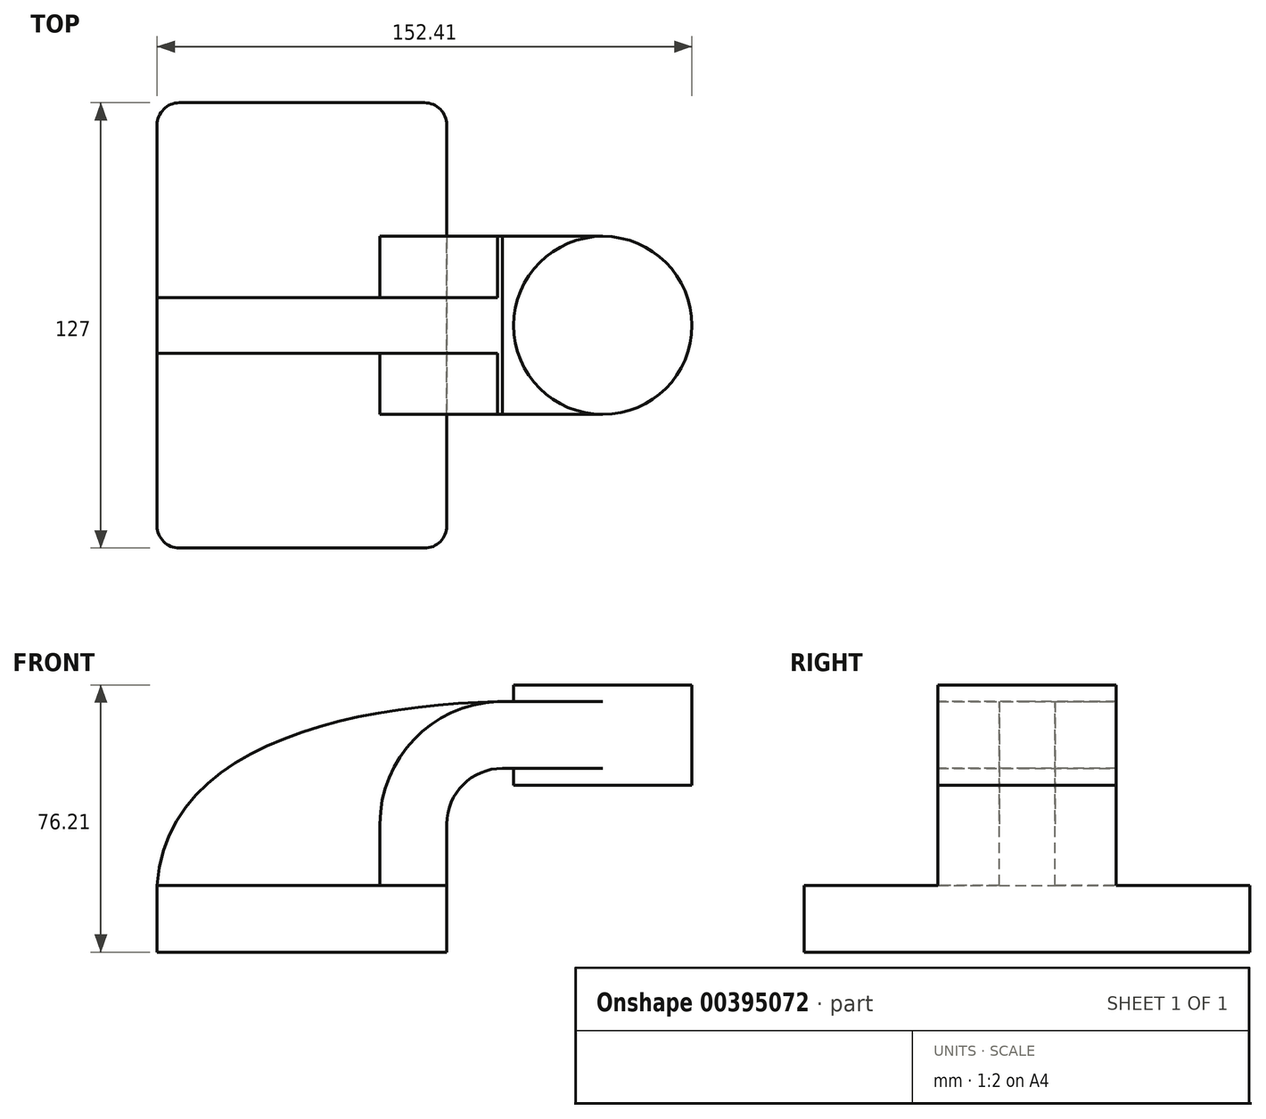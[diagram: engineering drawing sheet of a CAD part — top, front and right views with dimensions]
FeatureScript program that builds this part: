
annotation { "Feature Type Name" : "Feature", "Feature Type Description" : "" }
export const myFeature = defineFeature(function(context is Context, id is Id, definition is map)
    precondition{}
    {
        {
            var Q0;
            Q0=qCreatedBy(makeId("Front.planeOp"),FACE);
            var sketch = newSketch(context, id + "F0", { "sketchPlane" : qUnion([Q0])});
            skLineSegment(sketch, "E0.bottom", {"start": v(41.28, -9.52) * mm, "end": v(-41.27, -9.52) * mm});
            skLineSegment(sketch, "E0.top", {"start": v(41.27, 9.53) * mm, "end": v(-41.28, 9.53) * mm});
            skLineSegment(sketch, "E0.left", {"start": v(41.28, -9.52) * mm, "end": v(41.28, 9.53) * mm});
            skLineSegment(sketch, "E0.right", {"start": v(-41.27, -9.52) * mm, "end": v(-41.28, 9.52) * mm});
            skPoint(sketch, "E0.middle", {"position": v(0, 0) * mm});
            skLineSegment(sketch, "E1.bottom", {"start": v(111.12, 66.68) * mm, "end": v(60.32, 66.68) * mm});
            skLineSegment(sketch, "E1.top", {"start": v(111.12, 38.1) * mm, "end": v(60.33, 38.1) * mm});
            skLineSegment(sketch, "E1.left", {"start": v(111.12, 66.68) * mm, "end": v(111.12, 38.1) * mm});
            skLineSegment(sketch, "E1.right", {"start": v(60.32, 66.68) * mm, "end": v(60.33, 38.1) * mm});
            skPoint(sketch, "E1.middle", {"position": v(85.73, 52.39) * mm});
            skLineSegment(sketch, "E2", {"start": v(41.27, 9.53) * mm, "end": v(41.27, 27) * mm});
            skArc(sketch, "E3", {"start": v(41.27, 27) * mm, "mid": v(45.92, 38.23) * mm, "end": v(57.15, 42.88) * mm});
            skLineSegment(sketch, "E4", {"start": v(57.15, 42.88) * mm, "end": v(85.72, 42.88) * mm});
            skLineSegment(sketch, "E5.0", {"start": v(57.15, 61.93) * mm, "end": v(85.72, 61.93) * mm});
            skArc(sketch, "E5.1", {"start": v(22.22, 27) * mm, "mid": v(32.45, 51.7) * mm, "end": v(57.15, 61.93) * mm});
            skLineSegment(sketch, "E5.2", {"start": v(22.22, 9.53) * mm, "end": v(22.22, 27) * mm});
            skLineSegment(sketch, "E6", {"start": v(85.72, 38.1) * mm, "end": v(85.72, 66.68) * mm});
            skFitSpline(sketch, "E7", {"points": [v(-41.28, 9.52) * mm, v(57.15, 61.93) * mm], "startDerivative": vector(7.4, 121.11) * mm, "endDerivative": vector(126.5, 2.33) * mm});
            skSolve(sketch);
        }
        {
            var Q0;
            Q0=makeQuery(id+"F0.imprint","IMPRINT",FACE,{"disambiguationData":[TD([[makeQuery(id+"F0.imprint","IMPRINT",EDGE,{"derivedFrom":sQuery(id+"F0.wireOp",EDGE,"E0.bottom")}),-1.0]])]});
            extrude(context, id + "F1", {"entities" : qUnion([Q0]), "endBound" : BoundingType.SYMMETRIC, "oppositeDirection" : true, "depth" : 127 * mm});
        }
        {
            var Q0;
            {var subQ1=sQuery(id+"F0.wireOp",EDGE,"E2");Q0=makeQuery(id+"F0.imprint","IMPRINT",FACE,{"disambiguationData":[TD([[makeQuery(id+"F0.imprint","IMPRINT",EDGE,{"derivedFrom":subQ1}),1.0]])]});}
            var Q1;
            {var subQ0=sQuery(id+"F0.wireOp",EDGE,"E5.0");var subQ1=sQuery(id+"F0.wireOp",EDGE,"E1.right");var subQ2=makeQuery(id+"F0.imprint","INTERSECT",VERTEX,{"derivedFrom":[subQ1,subQ0]});Q1=makeQuery(id+"F0.imprint","IMPRINT",FACE,{"disambiguationData":[TD([[makeQuery(id+"F0.imprint","IMPRINT",EDGE,{"disambiguationData":[TD([[subQ2,-1.0]])],"derivedFrom":subQ1}),1.0]])]});}
            extrude(context, id + "F2", {"entities" : qUnion([Q0, Q1]), "operationType" : NewBodyOperationType.ADD, "endBound" : BoundingType.SYMMETRIC, "depth" : 50.8 * mm});
        }
        {
            var Q0;
            {var subQ3=sQuery(id+"F0.wireOp",EDGE,"E5.2");Q0=makeQuery(id+"F0.imprint","IMPRINT",FACE,{"disambiguationData":[TD([[makeQuery(id+"F0.imprint","IMPRINT",EDGE,{"derivedFrom":subQ3}),1.0]])]});}
            extrude(context, id + "F3", {"entities" : qUnion([Q0]), "operationType" : NewBodyOperationType.ADD, "endBound" : BoundingType.SYMMETRIC, "depth" : 15.88 * mm});
        }
        {
            var Q0;
            {var subQ0=sQuery(id+"F0.wireOp",EDGE,"E1.left");Q0=makeQuery(id+"F0.imprint","IMPRINT",FACE,{"disambiguationData":[TD([[makeQuery(id+"F0.imprint","IMPRINT",EDGE,{"derivedFrom":subQ0}),-1.0]])]});}
            var Q1;
            Q1=sQuery(id+"F0.wireOp",EDGE,"E6");
            revolve(context, id + "F4", {"operationType" : NewBodyOperationType.ADD, "entities" : qUnion([Q0]), "axis" : qUnion([Q1]), "revolveType" : RevolveType.FULL});
        }
        {
            var Q0;
            Q0=makeQuery(id+"F1.opExtrude","CAP_EDGE",EDGE,{"disambiguationData":[OSD([sQuery(id+"F0.wireOp",EDGE,"E0.left")])],"isStart":true});
            var Q1;
            Q1=makeQuery(id+"F1.opExtrude","CAP_EDGE",EDGE,{"disambiguationData":[OSD([sQuery(id+"F0.wireOp",EDGE,"E0.right")])],"isStart":true});
            var Q2;
            Q2=makeQuery(id+"F1.opExtrude","CAP_EDGE",EDGE,{"disambiguationData":[OSD([sQuery(id+"F0.wireOp",EDGE,"E0.left")])],"isStart":false});
            var Q3;
            Q3=makeQuery(id+"F1.opExtrude","CAP_EDGE",EDGE,{"disambiguationData":[OSD([sQuery(id+"F0.wireOp",EDGE,"E0.right")])],"isStart":false});
            fillet(context, id + "F5", {"entities" : qUnion([Q0, Q1, Q2, Q3]), "radius" : 6.35 * mm, "tangentPropagation" : true, "allowEdgeOverflow" : false});
        }
    });
